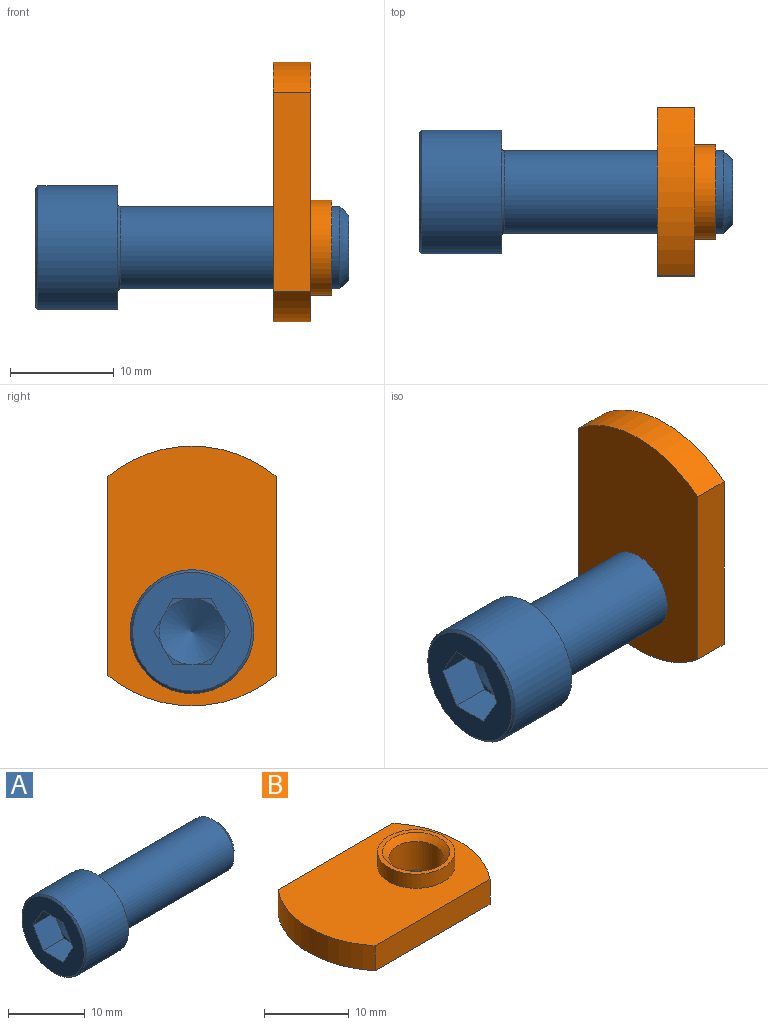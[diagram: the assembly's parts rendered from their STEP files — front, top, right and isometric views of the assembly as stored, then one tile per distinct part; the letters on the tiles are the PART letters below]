
ASSEMBLY  parts=2 mates=1
PART A: 21 faces, bbox 30.2x11.9x11.9 mm
  f0: plane 3.18x0.92mm, normal (-1,0,0), area 0.5mm2, adj f14,f15,f20
  f1: plane 2.75x1.59mm, normal (-1,0,0), area 0.5mm2, adj f13,f14,f20
  f2: plane 2.75x1.59mm, normal (-1,0,0), area 0.5mm2, adj f13,f18,f20
  f3: plane 3.18x0.92mm, normal (-1,0,0), area 0.5mm2, adj f17,f18,f20
  f4: plane 2.75x1.59mm, normal (-1,0,0), area 0.5mm2, adj f15,f16,f20
  f5: plane 11.44x11.44mm, normal (-1,0,0), area 67.8mm2, adj f6,f13,f14,f15,f16,f17,f18
  f6: cone r=5.72mm half-angle=45deg, axis (1,0,0), area 12.4mm2, adj f5,f7
  f7: cylinder r=5.96mm len=11.91mm, axis (1,0,0), area 287.7mm2, adj f6,f8
  f8: plane 11.91x11.91mm, normal (1,0,0), area 55.9mm2, adj f7,f9
  f9: torus R=4.21mm, axis (1,0,0), area 9.5mm2, adj f8,f10
  f10: cylinder r=3.97mm len=21.15mm, axis (1,0,0), area 527.3mm2, adj f9,f11
  f11: cone r=3.97mm half-angle=45deg, axis (-1,0,0), area 26.5mm2, adj f10,f12
  f12: plane 6.26x6.26mm, normal (1,0,0), area 30.8mm2, adj f11
  f13: plane 3.84x3.67mm, normal (0,0,-1), area 14.1mm2, adj f1,f2,f5,f14,f18
  f14: plane 3.84x3.18mm, normal (0,0.87,-0.5), area 14.1mm2, adj f0,f1,f5,f13,f15
  f15: plane 3.84x3.18mm, normal (0,0.87,0.5), area 14.1mm2, adj f0,f4,f5,f14,f16
  f16: plane 3.84x3.67mm, normal (0,0,1), area 14.1mm2, adj f4,f5,f15,f17,f19
  f17: plane 3.84x3.18mm, normal (0,-0.87,0.5), area 14.1mm2, adj f3,f5,f16,f18,f19
  f18: plane 3.84x3.18mm, normal (0,-0.87,-0.5), area 14.1mm2, adj f2,f3,f5,f13,f17
  f19: plane 2.75x1.59mm, normal (-1,0,0), area 0.5mm2, adj f16,f17,f20
  f20: cone r=3.17mm half-angle=60deg, axis (-1,0,0), area 36.6mm2, adj f0,f1,f2,f3,f4,f19
PART B: 11 faces, bbox 25x16.2x5.6 mm
  f0: plane 19.17x3.61mm, normal (0,1,0), area 69.2mm2, adj f1,f3,f4,f5
  f1: cylinder r=12.7mm len=16.18mm, axis (0,0,-1), area 63.3mm2, adj f0,f2,f4,f5
  f2: plane 19.17x3.61mm, normal (0,-1,0), area 69.2mm2, adj f1,f3,f4,f5
  f3: cylinder r=12.7mm len=16.18mm, axis (0,0,-1), area 63.3mm2, adj f0,f2,f4,f5
  f4: plane 24.99x16.18mm, normal (0,0,1), area 309.3mm2, adj f0,f1,f2,f3,f6
  f5: plane 24.99x16.18mm, normal (0,0,-1), area 325.1mm2, adj f0,f1,f2,f3,f10
  f6: cylinder r=4.56mm len=9.12mm, axis (0,0,-1), area 58.2mm2, adj f4,f7
  f7: plane 9.12x9.12mm, normal (0,0,1), area 15.8mm2, adj f6,f8
  f8: cone r=3.97mm half-angle=45deg, axis (0,0,1), area 24.3mm2, adj f7,f9
  f9: cylinder r=3.21mm len=6.41mm, axis (0,0,-1), area 82.8mm2, adj f8,f10
  f10: cone r=3.21mm half-angle=45deg, axis (0,0,-1), area 24.3mm2, adj f5,f9
PLACE A at identity fixed
PLACE B rot(axis=(0,1,0),90deg) t=(16.79,0,0)mm
MATE fastened A.f6 <-> B.f6  axis (1,0,0) through (0,0,0)mm
